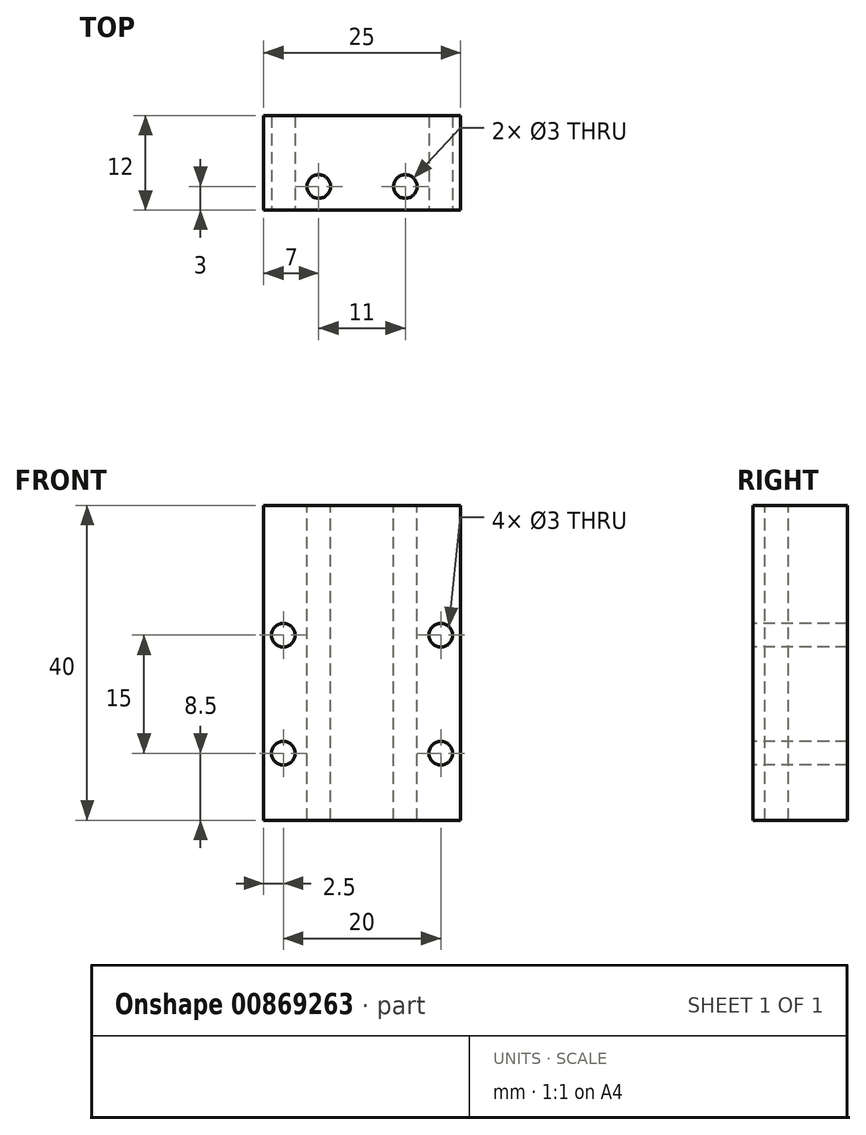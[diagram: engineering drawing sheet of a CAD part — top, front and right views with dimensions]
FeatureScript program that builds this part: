
annotation { "Feature Type Name" : "Feature", "Feature Type Description" : "" }
export const myFeature = defineFeature(function(context is Context, id is Id, definition is map)
    precondition{}
    {
        {
            var Q0;
            Q0=qCreatedBy(makeId("Top.planeOp"),FACE);
            var sketch = newSketch(context, id + "F0", { "sketchPlane" : qUnion([Q0])});
            skLineSegment(sketch, "E0.bottom", {"start": v(12.5, -6) * mm, "end": v(-12.5, -6) * mm});
            skLineSegment(sketch, "E0.top", {"start": v(12.5, 6) * mm, "end": v(-12.5, 6) * mm});
            skLineSegment(sketch, "E0.left", {"start": v(12.5, -6) * mm, "end": v(12.5, 6) * mm});
            skLineSegment(sketch, "E0.right", {"start": v(-12.5, -6) * mm, "end": v(-12.5, 6) * mm});
            skPoint(sketch, "E0.middle", {"position": v(0, 0) * mm});
            skSolve(sketch);
        }
        {
            var Q0;
            Q0=makeQuery(id+"F0.imprint","IMPRINT",FACE,{"disambiguationData":[TD([[makeQuery(id+"F0.imprint","IMPRINT",EDGE,{"derivedFrom":sQuery(id+"F0.wireOp",EDGE,"E0.bottom")}),-1.0]])]});
            extrude(context, id + "F1", {"entities" : qUnion([Q0]), "depth" : 40 * mm, "offsetDistance" : 25 * mm});
        }
        {
            var Q0;
            Q0=makeQuery(id+"F1.opExtrude","SWEPT_FACE",FACE,{"disambiguationData":[OSD([sQuery(id+"F0.wireOp",EDGE,"E0.bottom")])]});
            var sketch = newSketch(context, id + "F2", { "sketchPlane" : qUnion([Q0])});
            skLineSegment(sketch, "E1.bottom", {"start": v(10, 8.5) * mm, "end": v(-10, 8.5) * mm});
            skLineSegment(sketch, "E1.top", {"start": v(10, 23.5) * mm, "end": v(-10, 23.5) * mm});
            skLineSegment(sketch, "E1.left", {"start": v(10, 8.5) * mm, "end": v(10, 23.5) * mm});
            skLineSegment(sketch, "E1.right", {"start": v(-10, 8.5) * mm, "end": v(-10, 23.5) * mm});
            skPoint(sketch, "E1.middle", {"position": v(0, 16) * mm});
            skSolve(sketch);
        }
        {
            var Q0;
            Q0=sQuery(id+"F2.wireOp",VERTEX,"E1.top.end");
            var Q1;
            Q1=sQuery(id+"F2.wireOp",VERTEX,"E1.bottom.end");
            var Q2;
            Q2=sQuery(id+"F2.wireOp",VERTEX,"E1.bottom.start");
            var Q3;
            Q3=sQuery(id+"F2.wireOp",VERTEX,"E1.top.start");
            var Q4;
            Q4=makeQuery(id+"F1.opExtrude","SWEPT_BODY",BODY,{"disambiguationData":[OSD([sQuery(id+"F0.wireOp",EDGE,"E0.bottom"),sQuery(id+"F0.wireOp",EDGE,"E0.top"),sQuery(id+"F0.wireOp",EDGE,"E0.left"),sQuery(id+"F0.wireOp",EDGE,"E0.right")])]});
            hole(context, id + "F3", {"style" : HoleStyle.SIMPLE, "endStyle" : HoleEndStyle.THROUGH, "holeDiameter" : 3 * mm, "majorDiameter" : 5 * mm, "isTappedThrough" : true, "tappedDepth" : 12 * mm, "tapClearance" : 3, "locations" : qUnion([Q0, Q1, Q2, Q3]), "scope" : qUnion([Q4])});
        }
        {
            var Q0;
            Q0=makeQuery(id+"F1.opExtrude","CAP_FACE",FACE,{"disambiguationData":[OSD([sQuery(id+"F0.wireOp",EDGE,"E0.bottom"),sQuery(id+"F0.wireOp",EDGE,"E0.top"),sQuery(id+"F0.wireOp",EDGE,"E0.left"),sQuery(id+"F0.wireOp",EDGE,"E0.right")])],"isStart":false});
            var sketch = newSketch(context, id + "F4", { "sketchPlane" : qUnion([Q0])});
            skLineSegment(sketch, "E2.bottom", {"start": v(5.5, -3) * mm, "end": v(-5.5, -3) * mm});
            skLineSegment(sketch, "E2.top", {"start": v(5.5, -3) * mm, "end": v(-5.5, -3) * mm});
            skLineSegment(sketch, "E2.left", {"start": v(5.5, -3) * mm, "end": v(5.5, -3) * mm});
            skLineSegment(sketch, "E2.right", {"start": v(-5.5, -3) * mm, "end": v(-5.5, -3) * mm});
            skPoint(sketch, "E2.middle", {"position": v(0, -3) * mm});
            skSolve(sketch);
        }
        {
            var Q0;
            Q0=sQuery(id+"F4.wireOp",VERTEX,"lKaOIARr-kOwF-oPWo-7UP9-7snXTRkEfXOH.end");
            var Q1;
            Q1=sQuery(id+"F4.wireOp",VERTEX,"uVfzGBQb-WCtj-hkuz-ru9Z-B8ajEqC56ZhA.end");
            var Q2;
            Q2=sQuery(id+"F4.wireOp",VERTEX,"E2.top.end");
            var Q3;
            Q3=sQuery(id+"F4.wireOp",VERTEX,"E2.bottom.start");
            var Q4;
            Q4=sQuery(id+"F4.wireOp",VERTEX,"E2.bottom.end");
            var Q5;
            Q5=sQuery(id+"F4.wireOp",VERTEX,"E2.top.start");
            var Q6;
            Q6=makeQuery(id+"F1.opExtrude","SWEPT_BODY",BODY,{"disambiguationData":[OSD([sQuery(id+"F0.wireOp",EDGE,"E0.bottom"),sQuery(id+"F0.wireOp",EDGE,"E0.top"),sQuery(id+"F0.wireOp",EDGE,"E0.left"),sQuery(id+"F0.wireOp",EDGE,"E0.right")])]});
            hole(context, id + "F5", {"style" : HoleStyle.SIMPLE, "endStyle" : HoleEndStyle.THROUGH, "holeDiameter" : 3 * mm, "majorDiameter" : 5 * mm, "isTappedThrough" : true, "tappedDepth" : 12 * mm, "tapClearance" : 3, "locations" : qUnion([Q0, Q1, Q2, Q3, Q4, Q5]), "scope" : qUnion([Q6])});
        }
    });
